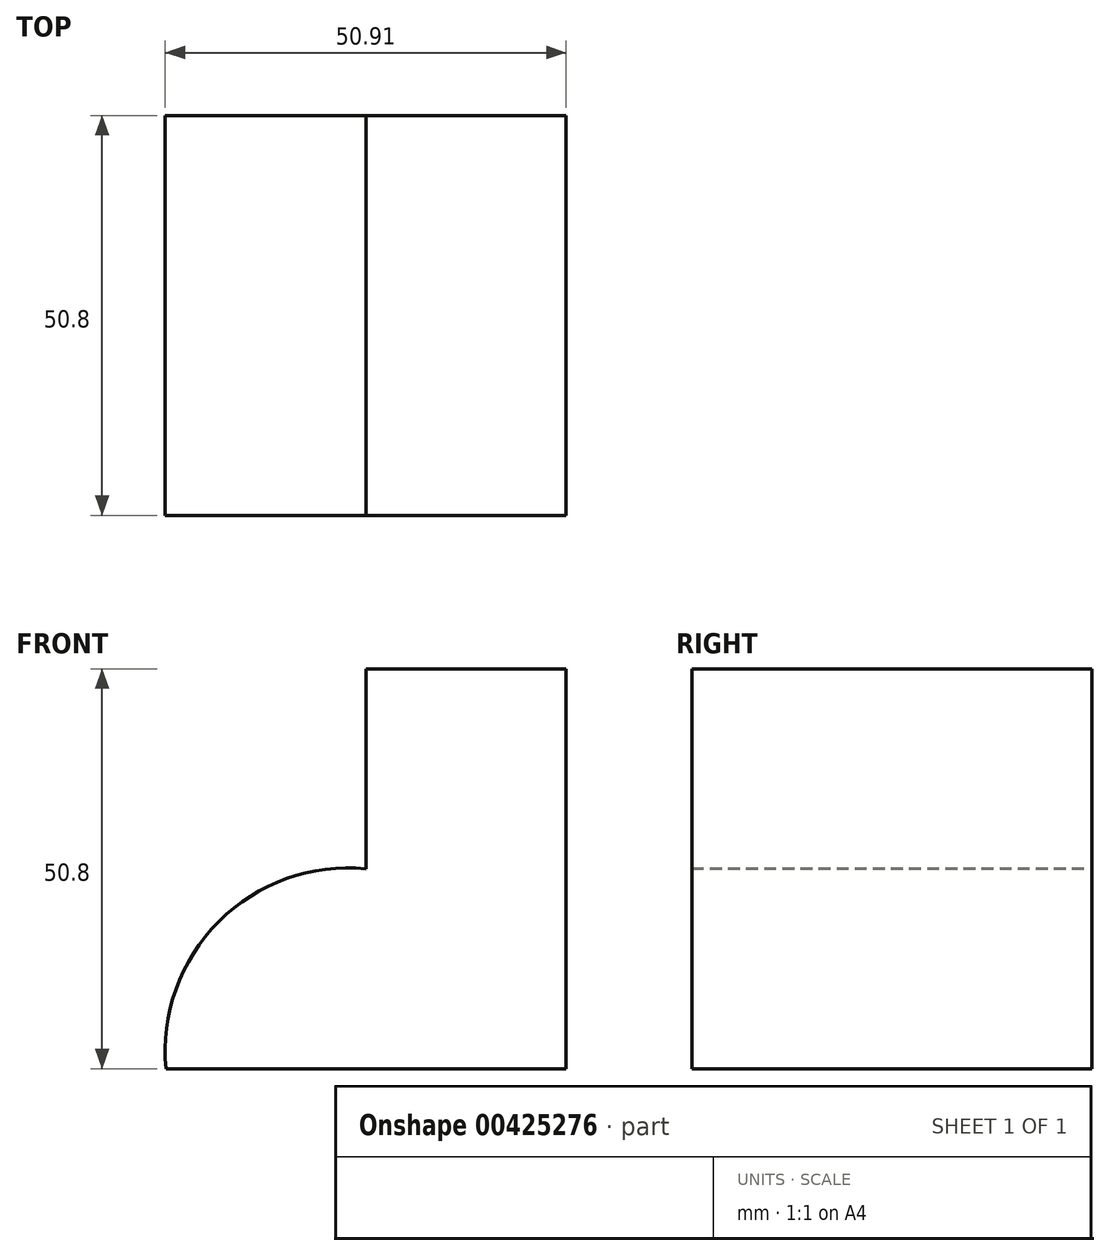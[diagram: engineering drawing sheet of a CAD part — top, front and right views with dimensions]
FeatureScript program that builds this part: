
annotation { "Feature Type Name" : "Feature", "Feature Type Description" : "" }
export const myFeature = defineFeature(function(context is Context, id is Id, definition is map)
    precondition{}
    {
        {
            var Q0;
            Q0=qCreatedBy(makeId("Front.planeOp"),FACE);
            var sketch = newSketch(context, id + "F0", { "sketchPlane" : qUnion([Q0])});
            skLineSegment(sketch, "E0", {"start": v(-25.4, 50.8) * mm, "end": v(0, 50.8) * mm});
            skLineSegment(sketch, "E1", {"start": v(0, 50.8) * mm, "end": v(0, 0) * mm});
            skLineSegment(sketch, "E2", {"start": v(0, 0) * mm, "end": v(-50.8, 0) * mm});
            skLineSegment(sketch, "E3", {"start": v(-25.4, 50.8) * mm, "end": v(-25.4, 25.4) * mm});
            skArc(sketch, "E4", {"start": v(-25.4, 25.4) * mm, "mid": v(-44.1, 18.7) * mm, "end": v(-50.8, 0) * mm});
            skSolve(sketch);
        }
        {
            var Q0;
            Q0 = qSketchRegion(id + "F0", true);
            extrude(context, id + "F1", {"entities" : qUnion([Q0]), "depth" : 50.8 * mm});
        }
    });
